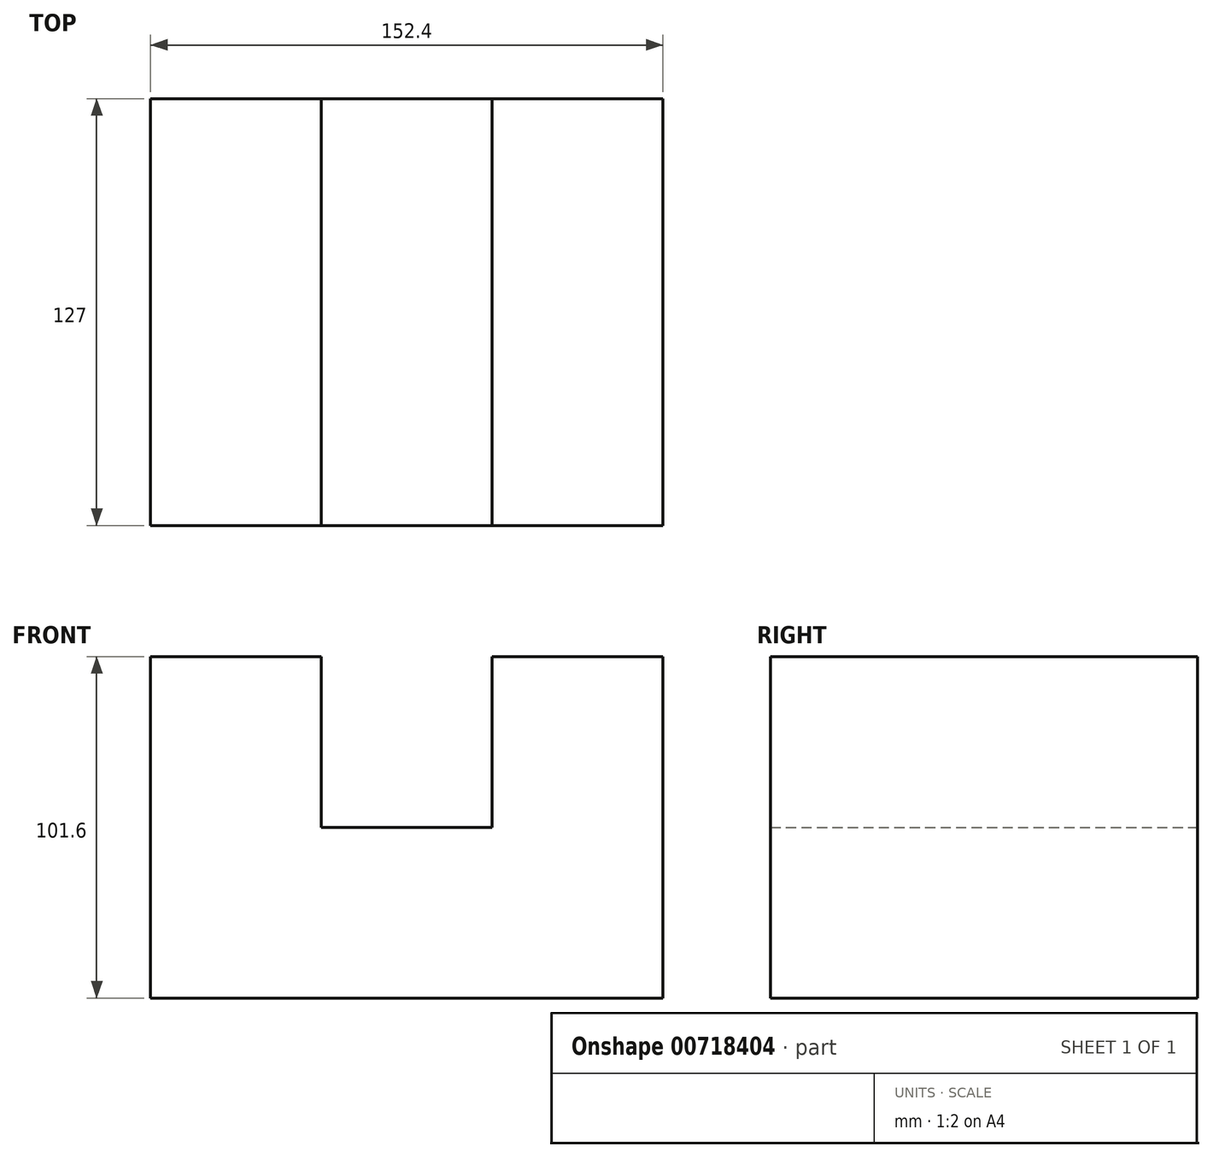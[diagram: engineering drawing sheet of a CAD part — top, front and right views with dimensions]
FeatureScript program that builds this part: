
annotation { "Feature Type Name" : "Feature", "Feature Type Description" : "" }
export const myFeature = defineFeature(function(context is Context, id is Id, definition is map)
    precondition{}
    {
        {
            var Q0;
            Q0=qCreatedBy(makeId("Front.planeOp"),FACE);
            var sketch = newSketch(context, id + "F0", { "sketchPlane" : qUnion([Q0])});
            skLineSegment(sketch, "E0", {"start": v(-93.3, -21.83) * mm, "end": v(59.1, -21.83) * mm});
            skLineSegment(sketch, "E1", {"start": v(59.1, -21.83) * mm, "end": v(59.1, 79.77) * mm});
            skLineSegment(sketch, "E2", {"start": v(59.1, 79.77) * mm, "end": v(8.3, 79.77) * mm});
            skLineSegment(sketch, "E3", {"start": v(8.3, 79.77) * mm, "end": v(8.3, 28.97) * mm});
            skLineSegment(sketch, "E4", {"start": v(8.3, 28.97) * mm, "end": v(-42.5, 28.97) * mm});
            skLineSegment(sketch, "E5", {"start": v(-42.5, 28.97) * mm, "end": v(-42.5, 79.77) * mm});
            skLineSegment(sketch, "E6", {"start": v(-93.3, 79.77) * mm, "end": v(-42.5, 79.77) * mm});
            skLineSegment(sketch, "E7", {"start": v(-93.3, -21.83) * mm, "end": v(-93.3, 79.77) * mm});
            skSolve(sketch);
        }
        {
            var Q0;
            Q0=makeQuery(id+"F0.imprint","IMPRINT",FACE,{"disambiguationData":[TD([[makeQuery(id+"F0.imprint","IMPRINT",EDGE,{"derivedFrom":sQuery(id+"F0.wireOp",EDGE,"E0")}),1.0]])]});
            extrude(context, id + "F1", {"entities" : qUnion([Q0]), "depth" : 127 * mm, "offsetDistance" : 25.4 * mm});
        }
    });
